# Revit family: P200921MX-066c_MVW6230RHW
name_source: partatom
category: Specialty Equipment
units: mm (PartAtom-declared; Revit-internal decimal feet)

## family parameters
Always vertical = No
Cut with Voids When Loaded = No
Enable Cutting in Views = No
Maintain Annotation Orientation = No
Part Type = Normal
Room Calculation Point = No
Round Connector Dimension = Use Diameter
Shared = No
Work Plane-Based = No

## types (1)
- MVW6230RHW
    Accent Material = ARCAT - Plastic - Gray
    Amps = 0 A
    Back Panel Material = ARCAT - Metal - Aluminum
    Body Material = ARCAT - Metal - Steel - White
    Clearance Material = ARCAT - Clearance
    Default Elevation = 0"
    Depth = 27 7/8"
    Description = Smart Capable Top Load Washer with Extra Power Button - 4.7 cu. ft.
    Dimension Guide = https://www.whirlpool.com
    Display Material = ARCAT - Glass - Tempered - Dark - Black
    Display Panel Material = ARCAT - Metal - Steel - Dark - Gray
    Door Material = ARCAT - Metal - Steel - White
    Energy Guide = https://whirlpool.com
    Family Name = Laundry
    Feature 1 = Most Powerful Cleaning in its class driven by the Heavy Duty cycle with Extra Power button
    Feature 2 = Extra Power button
    Feature 3 = Smart capable appliance
    Glass Material = ARCAT - Glass - Tempered - Black
    Handle Material = ARCAT - Metal - Steel - Stainless
    Height = 41 9/16"
    Knob Material = ARCAT - Metal - Steel - Stainless
    Leg Material = ARCAT - Plastic - White
    Manufacturer = Maytag
    Model = MVW6230RHW
    Voltage = 0 V
    Width = 27 1/4"

## geometry (parser evidence)
native form markers: Sweep x6
no freeform markers — native parametric forms only
